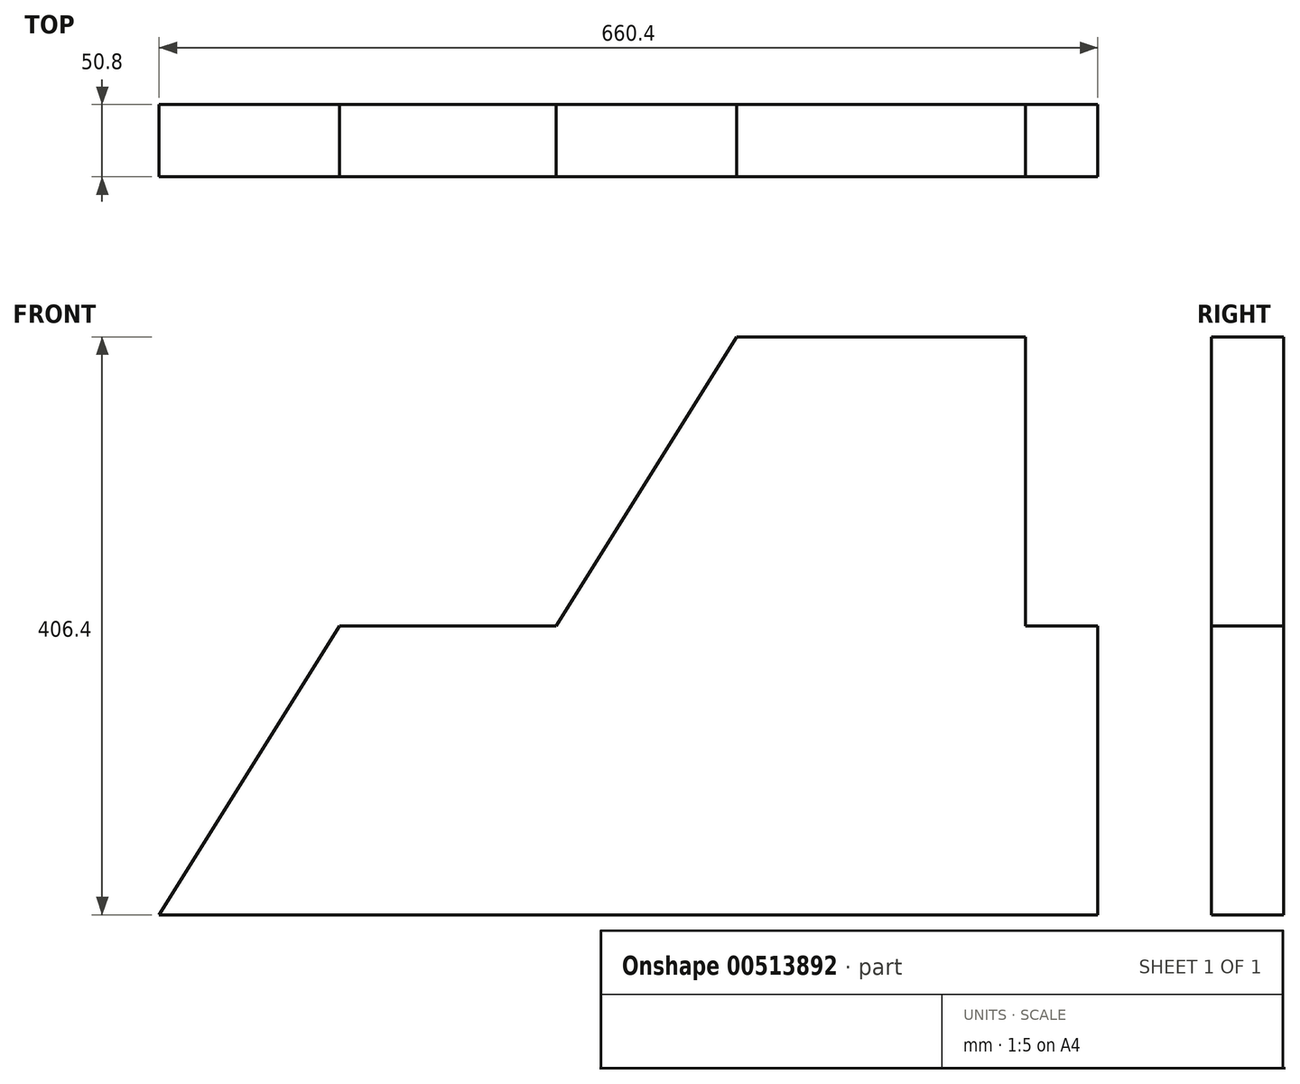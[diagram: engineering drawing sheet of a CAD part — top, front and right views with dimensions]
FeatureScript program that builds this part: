
annotation { "Feature Type Name" : "Feature", "Feature Type Description" : "" }
export const myFeature = defineFeature(function(context is Context, id is Id, definition is map)
    precondition{}
    {
        {
            var Q0;
            Q0=qCreatedBy(makeId("Front.planeOp"),FACE);
            var sketch = newSketch(context, id + "F0", { "sketchPlane" : qUnion([Q0])});
            skLineSegment(sketch, "E0", {"start": v(0, 0) * mm, "end": v(660.4, 0) * mm});
            skLineSegment(sketch, "E1", {"start": v(660.4, 0) * mm, "end": v(660.4, 203.2) * mm});
            skLineSegment(sketch, "E2", {"start": v(660.4, 203.2) * mm, "end": v(609.6, 203.2) * mm});
            skLineSegment(sketch, "E3", {"start": v(609.6, 203.2) * mm, "end": v(609.6, 406.4) * mm});
            skLineSegment(sketch, "E4", {"start": v(609.6, 406.4) * mm, "end": v(406.4, 406.4) * mm});
            skLineSegment(sketch, "E5", {"start": v(406.4, 406.4) * mm, "end": v(279.4, 203.2) * mm});
            skLineSegment(sketch, "E6", {"start": v(279.4, 203.2) * mm, "end": v(127, 203.2) * mm});
            skLineSegment(sketch, "E7", {"start": v(0, 0) * mm, "end": v(127, 203.2) * mm});
            skSolve(sketch);
        }
        {
            var Q0;
            Q0=makeQuery(id+"F0.imprint","IMPRINT",FACE,{"disambiguationData":[TD([[makeQuery(id+"F0.imprint","IMPRINT",EDGE,{"derivedFrom":sQuery(id+"F0.wireOp",EDGE,"E0")}),1.0]])]});
            extrude(context, id + "F1", {"entities" : qUnion([Q0]), "depth" : 50.8 * mm, "offsetDistance" : 25.4 * mm});
        }
    });
